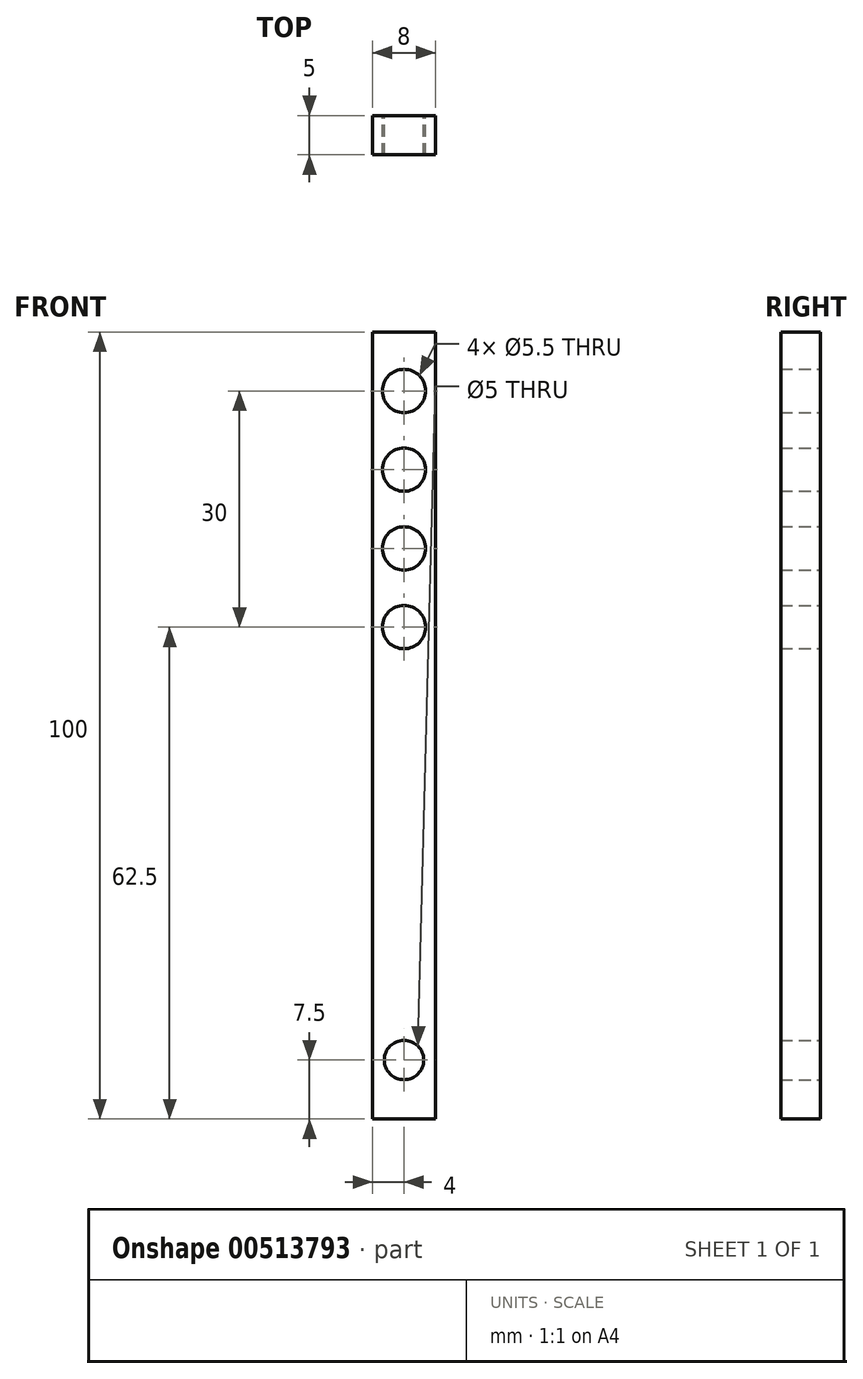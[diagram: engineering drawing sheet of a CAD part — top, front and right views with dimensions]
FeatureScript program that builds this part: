
annotation { "Feature Type Name" : "Feature", "Feature Type Description" : "" }
export const myFeature = defineFeature(function(context is Context, id is Id, definition is map)
    precondition{}
    {
        {
            var Q0;
            Q0=qCreatedBy(makeId("Front.planeOp"),FACE);
            var sketch = newSketch(context, id + "F0", { "sketchPlane" : qUnion([Q0])});
            skLineSegment(sketch, "E0.bottom", {"start": v(0, 0) * mm, "end": v(8, 0) * mm});
            skLineSegment(sketch, "E0.top", {"start": v(0, 100) * mm, "end": v(8, 100) * mm});
            skLineSegment(sketch, "E0.left", {"start": v(0, 0) * mm, "end": v(0, 100) * mm});
            skLineSegment(sketch, "E0.right", {"start": v(8, 0) * mm, "end": v(8, 100) * mm});
            skCircle(sketch, "E1", {"center": v(4, 7.5) * mm, "radius": 2.5 * mm});
            skCircle(sketch, "E2", {"center": v(4, 72.5) * mm, "radius": 2.75 * mm});
            skCircle(sketch, "E3", {"center": v(4, 82.5) * mm, "radius": 2.75 * mm});
            skCircle(sketch, "E4", {"center": v(4, 92.5) * mm, "radius": 2.75 * mm});
            skCircle(sketch, "E5", {"center": v(4, 62.5) * mm, "radius": 2.75 * mm});
            skSolve(sketch);
        }
        {
            var Q0;
            Q0=makeQuery(id+"F0.imprint","IMPRINT",FACE,{"disambiguationData":[TD([[makeQuery(id+"F0.imprint","IMPRINT",EDGE,{"derivedFrom":sQuery(id+"F0.wireOp",EDGE,"E0.bottom")}),1.0]])]});
            extrude(context, id + "F1", {"entities" : qUnion([Q0]), "depth" : 5 * mm, "offsetDistance" : 25 * mm});
        }
    });
